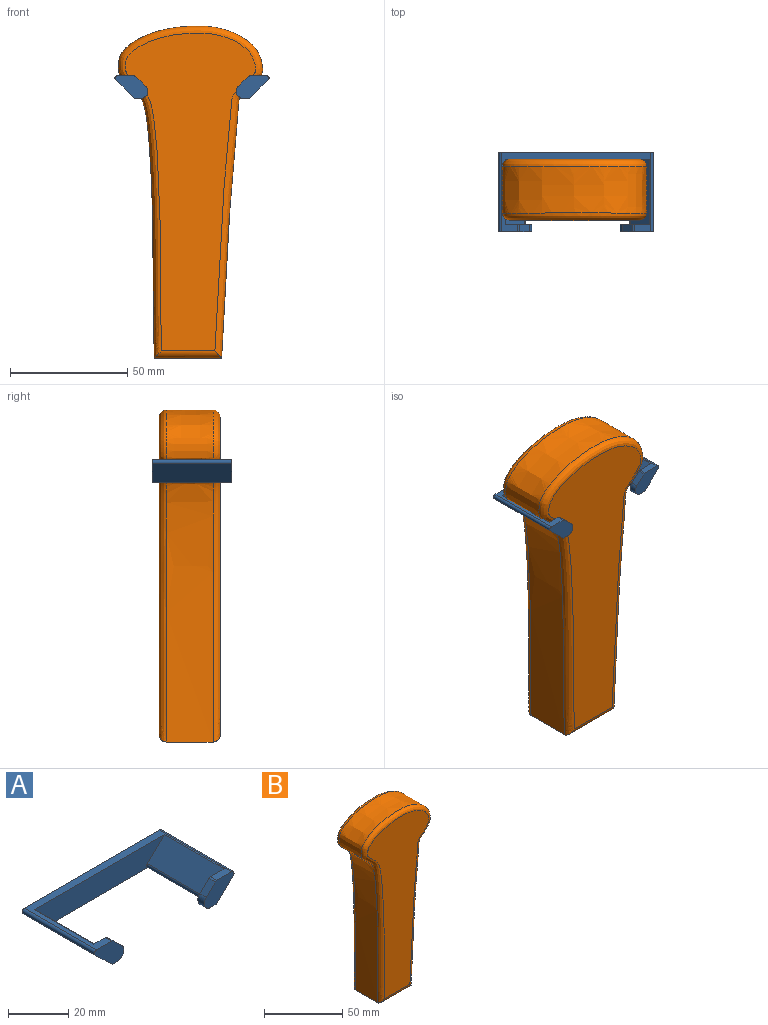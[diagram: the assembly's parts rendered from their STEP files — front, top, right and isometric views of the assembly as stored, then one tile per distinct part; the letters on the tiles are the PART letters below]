
ASSEMBLY  parts=2 mates=1
PART A: 22 faces, bbox 65.7x34x9.6 mm
  f0: plane 48.96x34mm, normal (0,0,-1), area 231.3mm2, adj f3,f4,f6,f7,f9,f10,f11,f13
  f1: plane 28x8.09mm, normal (0.7,0,0.72), area 315.6mm2, adj f2,f4,f10,f18
  f2: plane 63.74x34mm, normal (0,0,1), area 302.8mm2, adj f1,f4,f5,f7,f9,f10,f11,f13
  f3: plane 34x8.09mm, normal (-0.7,0,-0.72), area 383.2mm2, adj f0,f7,f9,f19
  f4: plane 61.29x9.57mm, normal (0,-1,0), area 494.7mm2, adj f0,f1,f2,f5,f16,f18
  f5: plane 28x8.09mm, normal (-0.7,0,0.72), area 315.6mm2, adj f2,f4,f11,f16
  f6: plane 34x8.09mm, normal (0.7,0,-0.72), area 383.2mm2, adj f0,f7,f13,f17
  f7: plane 65.74x9.57mm, normal (0,1,0), area 560.2mm2, adj f0,f2,f3,f6,f17,f19
  f8: plane 4.26x4.13mm, normal (0.7,0,0.72), area 17.8mm2, adj f9,f10,f14,f20
  f9: plane 13.99x9.57mm, normal (0,-1,0), area 82.9mm2, adj f0,f2,f3,f8,f14,f19,f20
  f10: plane 11.2x9.57mm, normal (0,1,0), area 44.7mm2, adj f0,f1,f2,f8,f14,f18,f20
  f11: plane 12.33x9.57mm, normal (0,1,0), area 55.4mm2, adj f0,f2,f5,f12,f15,f16,f21
  f12: plane 4.26x4.13mm, normal (-0.7,0,0.72), area 17.8mm2, adj f11,f13,f15,f21
  f13: plane 13.99x9.57mm, normal (0,-1,0), area 82.9mm2, adj f0,f2,f6,f12,f15,f17,f21
  f14: cylinder r=1mm len=3mm, axis (0,-1,0), area 2.3mm2, adj f2,f8,f9,f10
  f15: cylinder r=1mm len=3mm, axis (0,-1,0), area 2.3mm2, adj f2,f11,f12,f13
  f16: cylinder r=1mm len=28mm, axis (0,-1,0), area 66.4mm2, adj f0,f4,f5,f11
  f17: cylinder r=1mm len=34mm, axis (0,1,0), area 80.6mm2, adj f2,f6,f7,f13
  f18: cylinder r=1mm len=28mm, axis (0,1,0), area 66.4mm2, adj f0,f1,f4,f10
  f19: cylinder r=1mm len=34mm, axis (0,-1,0), area 80.6mm2, adj f2,f3,f7,f9
  f20: cylinder r=3mm len=5.15mm, axis (0,-1,0), area 21.3mm2, adj f0,f8,f9,f10
  f21: cylinder r=3mm len=5.15mm, axis (0,-1,0), area 21.3mm2, adj f0,f11,f12,f13
PART B: 11 faces, bbox 61.5x26x157.8 mm
  f0: extruded ~141.62x61.33mm, area 6647.8mm2, adj f1,f2,f6,f8
  f1: plane 28.81x20mm, normal (0,0,-1), area 576.1mm2, adj f0,f2,f7,f10
  f2: plane 20x0.57mm, normal (1,0,0), area 11.4mm2, adj f0,f1,f5,f9
  f3: plane 135.64x55.49mm, normal (0,-1,0), area 4182.1mm2, adj f8,f10
  f4: plane 135.64x55.49mm, normal (0,1,0), area 4137.4mm2, adj f6,f7
  f5: cylinder r=3mm len=1.8mm, axis (0,0,1), area 0.6mm2, adj f2,f6,f7
  f6: bspline ~152.56x61.49mm, area 1520mm2, adj f0,f4,f5,f7
  f7: cylinder r=3mm len=28.81mm, axis (1,0,0), area 123.3mm2, adj f1,f4,f5,f6
  f8: bspline ~157.76x61.49mm, area 1519.9mm2, adj f0,f3,f9,f10
  f9: cylinder r=3mm len=1.8mm, axis (0,0,-1), area 0.6mm2, adj f2,f8,f10
  f10: cylinder r=3mm len=28.81mm, axis (-1,0,0), area 123.3mm2, adj f1,f3,f8,f9
PLACE A at identity fixed
PLACE B t=(-0.7,0,-0.46)mm
MATE planar B.f4 <-> A.f4  axis (0,1,0) through (-0.51,0,4.21)mm
